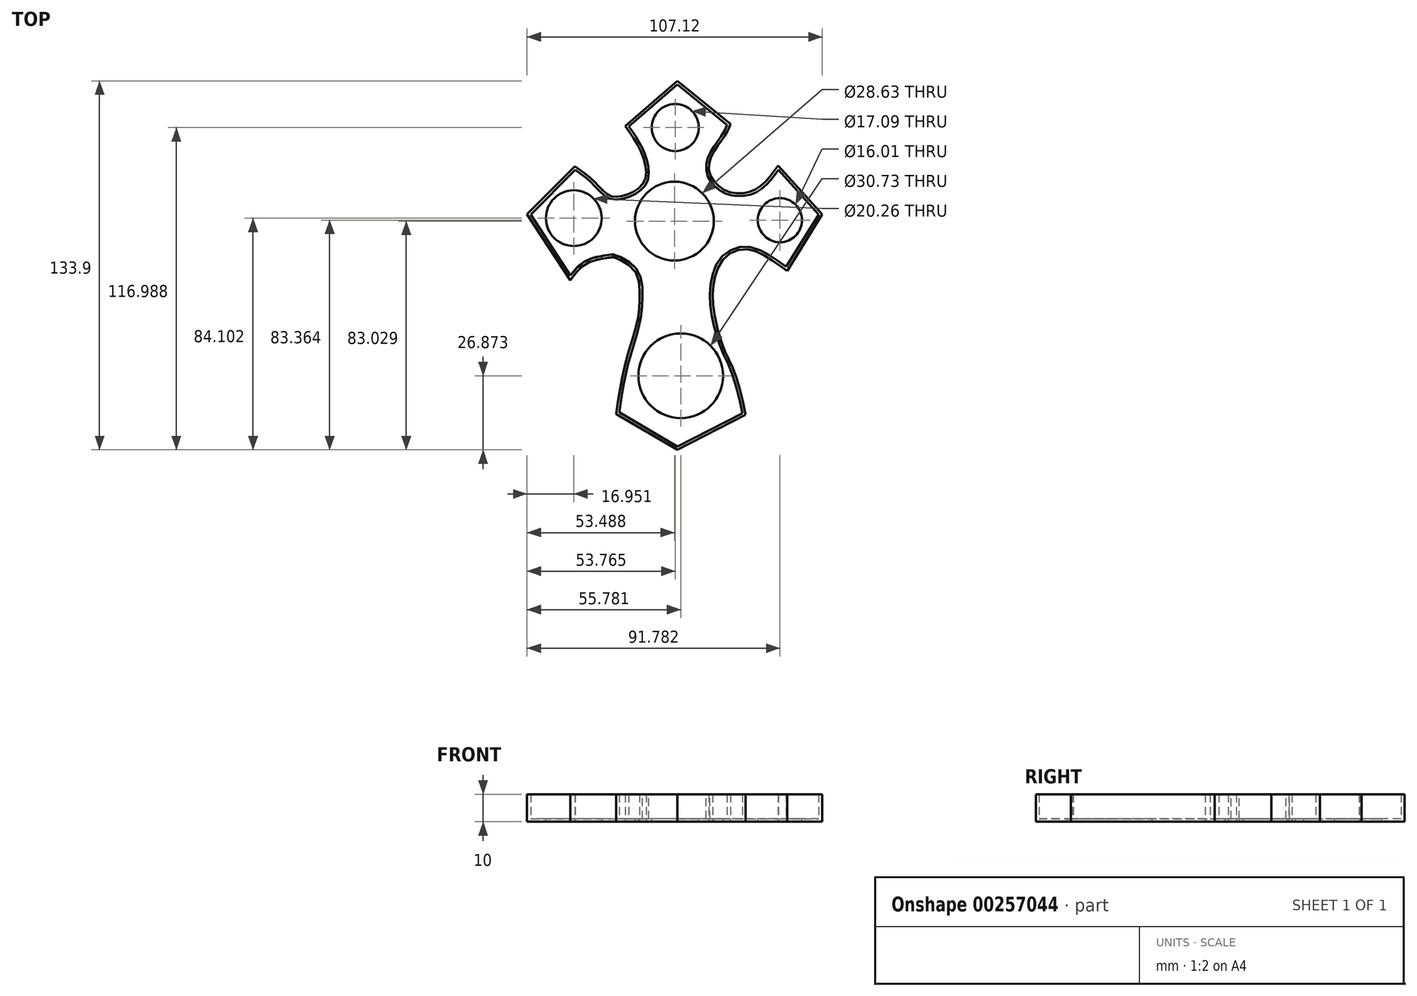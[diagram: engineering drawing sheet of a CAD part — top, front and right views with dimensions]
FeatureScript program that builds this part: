
annotation { "Feature Type Name" : "Feature", "Feature Type Description" : "" }
export const myFeature = defineFeature(function(context is Context, id is Id, definition is map)
    precondition{}
    {
        {
            var Q0;
            Q0=qCreatedBy(makeId("Top.planeOp"),FACE);
            var sketch = newSketch(context, id + "F0", { "sketchPlane" : qUnion([Q0])});
            skLineSegment(sketch, "E0", {"start": v(-16.98, 72.34) * mm, "end": v(-35.92, 56) * mm});
            skLineSegment(sketch, "E1", {"start": v(-16.98, 72.34) * mm, "end": v(2.29, 56.66) * mm});
            skLineSegment(sketch, "E2", {"start": v(19.6, 41.64) * mm, "end": v(35.6, 24) * mm});
            skLineSegment(sketch, "E3", {"start": v(35.6, 24) * mm, "end": v(22.86, 3.43) * mm});
            skLineSegment(sketch, "E4", {"start": v(7.84, -48.82) * mm, "end": v(-16.98, -61.56) * mm});
            skLineSegment(sketch, "E5", {"start": v(-16.98, -61.56) * mm, "end": v(-39.2, -48.5) * mm});
            skLineSegment(sketch, "E6", {"start": v(-55.85, 0) * mm, "end": v(-71.52, 24) * mm});
            skLineSegment(sketch, "E7", {"start": v(-71.52, 24) * mm, "end": v(-54.21, 41.31) * mm});
            skFitSpline(sketch, "E8", {"points": [v(-35.92, 56) * mm, v(-29.72, 45.56) * mm, v(-29.07, 35.76) * mm, v(-35.92, 30.86) * mm, v(-41.8, 30.86) * mm, v(-47.35, 36.09) * mm, v(-54.21, 41.31) * mm], "startDerivative": vector(35.73, -50.74) * mm, "endDerivative": vector(-43.2, 28.68) * mm});
            skFitSpline(sketch, "E9", {"points": [v(-55.85, 0) * mm, v(-49.97, 6.04) * mm, v(-41.6, 8.2) * mm, v(-40.4, 8.35) * mm, v(-40.17, 8.33) * mm, v(-32.98, 4.08) * mm, v(-30.7, -5.39) * mm, v(-31.35, -14.2) * mm, v(-35.92, -30.54) * mm, v(-39.2, -48.5) * mm], "startDerivative": vector(40.71, 54.04) * mm, "endDerivative": vector(-14.2, -97.94) * mm});
            skFitSpline(sketch, "E10", {"points": [v(7.84, -48.82) * mm, v(3.6, -32.82) * mm, v(0, -24.98) * mm, v(-3.92, -9.63) * mm, v(-3.6, 0) * mm, v(0, 8) * mm, v(7.84, 11.27) * mm, v(15.68, 8.33) * mm, v(22.86, 3.43) * mm], "startDerivative": vector(-25.56, 114.02) * mm, "endDerivative": vector(61.56, -44.16) * mm});
            skPoint(sketch, "E11.1.internal.snap0", {"position": v(27.6, 32.82) * mm});
            skPoint(sketch, "E11.2.internal.snap0", {"position": v(27.6, 32.82) * mm});
            skFitSpline(sketch, "E11", {"points": [v(19.6, 41.64) * mm, v(11.1, 32.82) * mm, v(0, 32.82) * mm, v(-5.55, 41.64) * mm, v(0, 52.1) * mm, v(2.29, 56.66) * mm], "startDerivative": vector(-33.53, -47.6) * mm, "endDerivative": vector(11.2, 28.64) * mm});
            skSolve(sketch);
        }
        {
            var Q0;
            Q0=makeQuery(id+"F0.imprint","IMPRINT",FACE,{"disambiguationData":[TD([[makeQuery(id+"F0.imprint","IMPRINT",EDGE,{"derivedFrom":sQuery(id+"F0.wireOp",EDGE,"E0")}),1.0]])]});
            extrude(context, id + "F1", {"entities" : qUnion([Q0]), "depth" : 10 * mm});
        }
        {
            var Q0;
            Q0=makeQuery(id+"F1.opExtrude","CAP_FACE",FACE,{"disambiguationData":[OSD([sQuery(id+"F0.wireOp",EDGE,"E0"),sQuery(id+"F0.wireOp",EDGE,"E1"),sQuery(id+"F0.wireOp",EDGE,"E2"),sQuery(id+"F0.wireOp",EDGE,"E3"),sQuery(id+"F0.wireOp",EDGE,"E4"),sQuery(id+"F0.wireOp",EDGE,"E5"),sQuery(id+"F0.wireOp",EDGE,"E6"),sQuery(id+"F0.wireOp",EDGE,"E7"),sQuery(id+"F0.wireOp",EDGE,"E8"),sQuery(id+"F0.wireOp",EDGE,"E9"),sQuery(id+"F0.wireOp",EDGE,"E10"),sQuery(id+"F0.wireOp",EDGE,"E11")])],"isStart":false});
            shell(context, id + "F2", {"entities" : qUnion([Q0]), "thickness" : 1 * mm});
        }
        {
            var Q0;
            Q0=makeQuery(id+"F2.opShell","OFFSET_FACE",FACE,{"disambiguationData":[OSD([sQuery(id+"F0.wireOp",EDGE,"E0"),sQuery(id+"F0.wireOp",EDGE,"E1"),sQuery(id+"F0.wireOp",EDGE,"E2"),sQuery(id+"F0.wireOp",EDGE,"E3"),sQuery(id+"F0.wireOp",EDGE,"E4"),sQuery(id+"F0.wireOp",EDGE,"E5"),sQuery(id+"F0.wireOp",EDGE,"E6"),sQuery(id+"F0.wireOp",EDGE,"E7"),sQuery(id+"F0.wireOp",EDGE,"E8"),sQuery(id+"F0.wireOp",EDGE,"E9"),sQuery(id+"F0.wireOp",EDGE,"E10"),sQuery(id+"F0.wireOp",EDGE,"E11")])]});
            var sketch = newSketch(context, id + "F3", { "sketchPlane" : qUnion([Q0])});
            skCircle(sketch, "E12", {"center": v(-18.03, 21.47) * mm, "radius": 14.31 * mm});
            skSolve(sketch);
        }
        {
            var Q0;
            Q0=makeQuery(id+"F3.imprint","IMPRINT",FACE,{"disambiguationData":[TD([[makeQuery(id+"F3.imprint","IMPRINT",EDGE,{"derivedFrom":sQuery(id+"F3.wireOp",EDGE,"E12")}),1.0]])]});
            extrude(context, id + "F4", {"entities" : qUnion([Q0]), "operationType" : NewBodyOperationType.REMOVE, "oppositeDirection" : true, "depth" : 25.4 * mm});
        }
        {
            var Q0;
            Q0=makeQuery(id+"F2.opShell","OFFSET_FACE",FACE,{"disambiguationData":[OSD([sQuery(id+"F0.wireOp",EDGE,"E0"),sQuery(id+"F0.wireOp",EDGE,"E1"),sQuery(id+"F0.wireOp",EDGE,"E2"),sQuery(id+"F0.wireOp",EDGE,"E3"),sQuery(id+"F0.wireOp",EDGE,"E4"),sQuery(id+"F0.wireOp",EDGE,"E5"),sQuery(id+"F0.wireOp",EDGE,"E6"),sQuery(id+"F0.wireOp",EDGE,"E7"),sQuery(id+"F0.wireOp",EDGE,"E8"),sQuery(id+"F0.wireOp",EDGE,"E9"),sQuery(id+"F0.wireOp",EDGE,"E10"),sQuery(id+"F0.wireOp",EDGE,"E11")])]});
            var sketch = newSketch(context, id + "F5", { "sketchPlane" : qUnion([Q0])});
            skCircle(sketch, "E13", {"center": v(-17.76, 55.43) * mm, "radius": 8.55 * mm});
            skCircle(sketch, "E14", {"center": v(19.68, 22.12) * mm, "radius": 9.32 * mm});
            skCircle(sketch, "E15", {"center": v(-16.96, -34.94) * mm, "radius": 14.81 * mm});
            skCircle(sketch, "E16", {"center": v(-56.14, 22.72) * mm, "radius": 9.4 * mm});
            skSolve(sketch);
        }
        {
            var Q0;
            Q0=makeQuery(id+"F5.imprint","IMPRINT",FACE,{"disambiguationData":[TD([[makeQuery(id+"F5.imprint","IMPRINT",EDGE,{"derivedFrom":sQuery(id+"F5.wireOp",EDGE,"E13")}),1.0]])]});
            extrude(context, id + "F6", {"entities" : qUnion([Q0]), "operationType" : NewBodyOperationType.REMOVE, "oppositeDirection" : true, "depth" : 25.4 * mm});
        }
        {
            var Q0;
            Q0=makeQuery(id+"F2.opShell","OFFSET_FACE",FACE,{"disambiguationData":[OSD([sQuery(id+"F0.wireOp",EDGE,"E0"),sQuery(id+"F0.wireOp",EDGE,"E1"),sQuery(id+"F0.wireOp",EDGE,"E2"),sQuery(id+"F0.wireOp",EDGE,"E3"),sQuery(id+"F0.wireOp",EDGE,"E4"),sQuery(id+"F0.wireOp",EDGE,"E5"),sQuery(id+"F0.wireOp",EDGE,"E6"),sQuery(id+"F0.wireOp",EDGE,"E7"),sQuery(id+"F0.wireOp",EDGE,"E8"),sQuery(id+"F0.wireOp",EDGE,"E9"),sQuery(id+"F0.wireOp",EDGE,"E10"),sQuery(id+"F0.wireOp",EDGE,"E11")])]});
            var sketch = newSketch(context, id + "F7", { "sketchPlane" : qUnion([Q0])});
            skCircle(sketch, "E17", {"center": v(20.26, 21.8) * mm, "radius": 8 * mm});
            skSolve(sketch);
        }
        {
            var Q0;
            Q0 = qSketchRegion(id + "F7", true);
            extrude(context, id + "F8", {"entities" : qUnion([Q0]), "operationType" : NewBodyOperationType.REMOVE, "oppositeDirection" : true, "depth" : 25.4 * mm});
        }
        {
            var Q0;
            Q0=makeQuery(id+"F2.opShell","OFFSET_FACE",FACE,{"disambiguationData":[OSD([sQuery(id+"F0.wireOp",EDGE,"E0"),sQuery(id+"F0.wireOp",EDGE,"E1"),sQuery(id+"F0.wireOp",EDGE,"E2"),sQuery(id+"F0.wireOp",EDGE,"E3"),sQuery(id+"F0.wireOp",EDGE,"E4"),sQuery(id+"F0.wireOp",EDGE,"E5"),sQuery(id+"F0.wireOp",EDGE,"E6"),sQuery(id+"F0.wireOp",EDGE,"E7"),sQuery(id+"F0.wireOp",EDGE,"E8"),sQuery(id+"F0.wireOp",EDGE,"E9"),sQuery(id+"F0.wireOp",EDGE,"E10"),sQuery(id+"F0.wireOp",EDGE,"E11")])]});
            var sketch = newSketch(context, id + "F9", { "sketchPlane" : qUnion([Q0])});
            skCircle(sketch, "E18", {"center": v(-15.74, -34.69) * mm, "radius": 15.36 * mm});
            skSolve(sketch);
        }
        {
            var Q0;
            Q0 = qSketchRegion(id + "F9", true);
            extrude(context, id + "F10", {"entities" : qUnion([Q0]), "operationType" : NewBodyOperationType.REMOVE, "oppositeDirection" : true, "depth" : 25.4 * mm});
        }
        {
            var Q0;
            Q0=makeQuery(id+"F2.opShell","OFFSET_FACE",FACE,{"disambiguationData":[OSD([sQuery(id+"F0.wireOp",EDGE,"E0"),sQuery(id+"F0.wireOp",EDGE,"E1"),sQuery(id+"F0.wireOp",EDGE,"E2"),sQuery(id+"F0.wireOp",EDGE,"E3"),sQuery(id+"F0.wireOp",EDGE,"E4"),sQuery(id+"F0.wireOp",EDGE,"E5"),sQuery(id+"F0.wireOp",EDGE,"E6"),sQuery(id+"F0.wireOp",EDGE,"E7"),sQuery(id+"F0.wireOp",EDGE,"E8"),sQuery(id+"F0.wireOp",EDGE,"E9"),sQuery(id+"F0.wireOp",EDGE,"E10"),sQuery(id+"F0.wireOp",EDGE,"E11")])]});
            var sketch = newSketch(context, id + "F11", { "sketchPlane" : qUnion([Q0])});
            skCircle(sketch, "E19", {"center": v(-54.57, 22.54) * mm, "radius": 10.13 * mm});
            skSolve(sketch);
        }
        {
            var Q0;
            Q0 = qSketchRegion(id + "F11", true);
            extrude(context, id + "F12", {"entities" : qUnion([Q0]), "operationType" : NewBodyOperationType.REMOVE, "oppositeDirection" : true, "depth" : 25.4 * mm});
        }
    });
